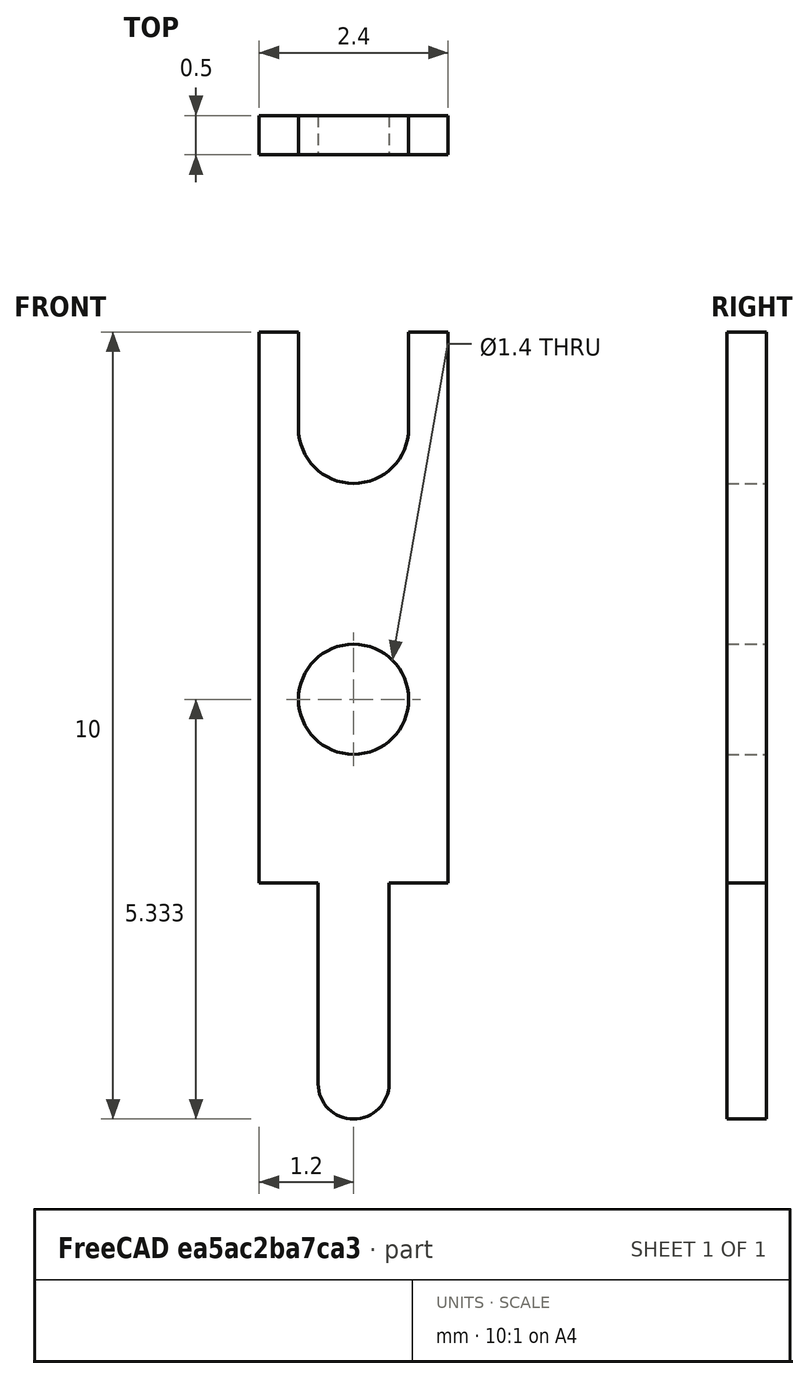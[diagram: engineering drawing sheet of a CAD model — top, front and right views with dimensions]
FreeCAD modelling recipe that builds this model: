
FCSTD DOCUMENT  (FreeCAD 0.17R12018 (Git))
Label: Pin_d0.9mm_L10.0mm_W2.4mm_FlatFork
License: All rights reserved
LicenseURL: http://en.wikipedia.org/wiki/All_rights_reserved
objects: Spreadsheet::Sheet×1, Sketcher::SketchObject×1, PartDesign::Pad×1
note: 3 computed .brp shape members not serialized (recipe doc carries the construction recipe); baked Part::Feature solids carry a one-line shape summary decoded from their .brp

FEATURE [Spreadsheet::Sheet] Spreadsheet  label="dimensions"
  cells = A1="L"; B1(L)=10; A2="Wtop"; B2(Wtop)=2.3999999999999999; A3="Wbottom"; B3(Wbottom)=0.90000000000000002; A4="Lbottom"; B4(Lbottom)=3; A5="Wfork"; B5(Wfork)=1.3999999999999999; A6="FractionFork"; B6(FractionFork)=0.25; A7="thick"; B7(thick)=0.5
FEATURE [Sketcher::SketchObject] Sketch
  MapMode = 5
  Placement = pos=(0,0,0) rot=(1,0,0;1.5708rad)
  expr: Constraints[44] = (dimensions.L - dimensions.Lbottom) * 0.66669999999999996
  expr: Constraints[43] = dimensions.Wfork / 2
  expr: Constraints[40] = dimensions.Wtop
  expr: Constraints[38] = dimensions.Wbottom
  expr: Constraints[39] = (dimensions.Wtop - dimensions.Wbottom) / 2
  expr: Constraints[37] = dimensions.Lbottom - dimensions.Wbottom / 2
  expr: Constraints[32] = dimensions.L - dimensions.Lbottom
  expr: Constraints[19] = dimensions.Wfork
  sketch-geometry (15):
    g0: LineSegment StartX=-1.2 StartY=7 StartZ=0 EndX=-1.2 EndY=0 EndZ=0
    g1: LineSegment StartX=-1.2 StartY=0 StartZ=0 EndX=-0.45 EndY=0 EndZ=0
    g2: LineSegment StartX=-0.45 StartY=0 StartZ=0 EndX=-0.45 EndY=-2.55 EndZ=0
    g3: LineSegment StartX=0.45 StartY=0 StartZ=0 EndX=0.45 EndY=-2.55 EndZ=0
    g4: LineSegment StartX=0.45 StartY=0 StartZ=0 EndX=1.2 EndY=0 EndZ=0
    g5: LineSegment StartX=1.2 StartY=0 StartZ=0 EndX=1.2 EndY=7 EndZ=0
    g6: LineSegment StartX=1.2 StartY=7 StartZ=0 EndX=0.7 EndY=7 EndZ=0
    g7: LineSegment StartX=0.7 StartY=7 StartZ=0 EndX=0.7 EndY=5.775 EndZ=0
    g8: LineSegment StartX=-0.7 StartY=5.775 StartZ=0 EndX=-0.7 EndY=7 EndZ=0
    g9: LineSegment StartX=-0.7 StartY=7 StartZ=0 EndX=-1.2 EndY=7 EndZ=0
    g10: ArcOfCircle CenterX=0 CenterY=-2.55 CenterZ=0 NormalX=0 NormalY=0 NormalZ=1 Radius=0.45 StartAngle=3.14159 EndAngle=6.28319
    g11: ArcOfCircle CenterX=0 CenterY=5.775 CenterZ=0 NormalX=0 NormalY=0 NormalZ=1 Radius=0.7 StartAngle=3.14159 EndAngle=6.28319
    g12: LineSegment [constr] StartX=-0.45 StartY=-2.55 StartZ=0 EndX=0.45 EndY=-2.55 EndZ=0
    g13: LineSegment [constr] StartX=-0.7 StartY=5.775 StartZ=0 EndX=0.7 EndY=5.775 EndZ=0
    g14: Circle CenterX=0 CenterY=2.3331 CenterZ=0 NormalX=0 NormalY=0 NormalZ=1 Radius=0.7
  constraints (45):
    c: PointOnObject(g3,g-1)
    c: Horizontal(g6)
    c: Vertical(g7)
    c: Vertical(g8)
    c: Coincident(g9,g0)
    c: Horizontal(g9)
    c: Equal(g9,g6)
    c: PointOnObject(g10,g-2)
    c: Coincident(g8,g9)
    c: Coincident(g6,g7)
    c: Coincident(g5,g6)
    c: Coincident(g11,g8)
    c: Coincident(g11,g7)
    c: Coincident(g12,g3)
    c: Coincident(g13,g8)
    c: Coincident(g13,g7)
    c: Horizontal(g13)
    c: PointOnObject(g11,g13)
    c: DistanceY(g8,g6) = 0
    c: DistanceX(g8,g6) = 1.4
    c: DistanceY(g8,g8) = 1.225
    c: Coincident(g12,g2)
    c: Coincident(g2,g10)
    c: Coincident(g3,g10)
    c: PointOnObject(g10,g12)
    c: Horizontal(g12)
    c: Vertical(g3)
    c: Vertical(g2)
    c: Horizontal(g1)
    c: Horizontal(g4)
    c: Vertical(g5)
    c: Vertical(g0)
    c: DistanceY(g5,g5) = 7
    c: Coincident(g5,g4)
    c: Coincident(g0,g1)
    c: Coincident(g4,g3)
    c: Coincident(g1,g2)
    c: DistanceY(g3,g3) = 2.55
    c: DistanceX(g2,g3) = 0.9
    c: DistanceX(g1,g1) = 0.75
    c: DistanceX(g0,g5) = 2.4
    c: PointOnObject(g1,g-1)
    c: PointOnObject(g14,g-2)
    c: Radius(g14) = 0.7
    c: DistanceY(g14,g8) = 4.6669
FEATURE [PartDesign::Pad] Pad  label="Pin_d0.9mm_L10.0mm_W2.4mm_FlatFork"
  Length = 0.5
  Length2 = 100
  Midplane = true
  Placement = pos=(0,0,0) rot=(1,0,0;1.5708rad)
  Profile = -> Sketch
  Type = 0
  expr: Length = dimensions.thick
